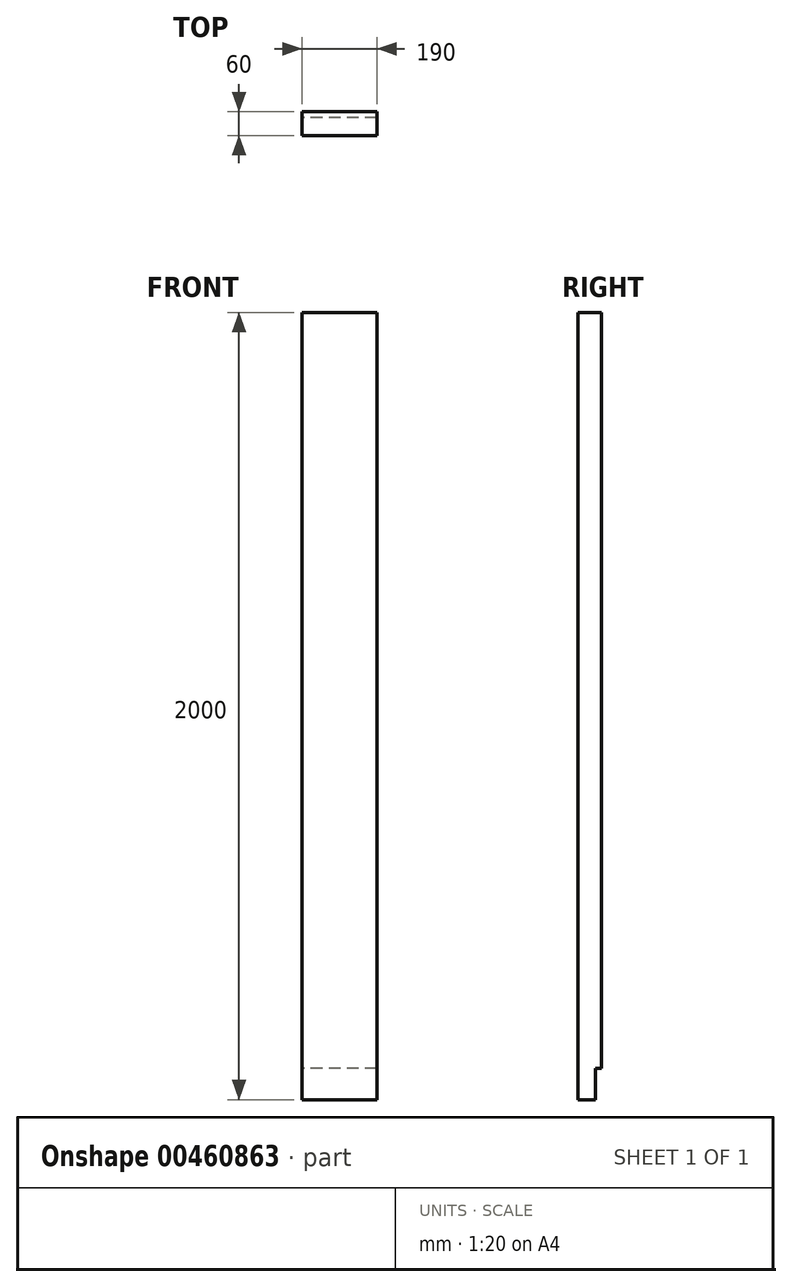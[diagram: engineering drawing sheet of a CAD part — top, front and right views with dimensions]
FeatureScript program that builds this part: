
annotation { "Feature Type Name" : "Feature", "Feature Type Description" : "" }
export const myFeature = defineFeature(function(context is Context, id is Id, definition is map)
    precondition{}
    {
        {
            var Q0;
            Q0=qCreatedBy(makeId("Front.planeOp"),FACE);
            var sketch = newSketch(context, id + "F0", { "sketchPlane" : qUnion([Q0])});
            skLineSegment(sketch, "E0.bottom", {"start": v(190, -3224.72) * mm, "end": v(0, -3224.72) * mm});
            skLineSegment(sketch, "E0.top", {"start": v(190, -5224.72) * mm, "end": v(0, -5224.72) * mm});
            skLineSegment(sketch, "E0.left", {"start": v(190, -3224.72) * mm, "end": v(190, -5224.72) * mm});
            skLineSegment(sketch, "E0.right", {"start": v(0, -3224.72) * mm, "end": v(0, -5224.72) * mm});
            skSolve(sketch);
        }
        {
            var Q0;
            Q0=makeQuery(id+"F0.imprint","IMPRINT",FACE,{"disambiguationData":[TD([[makeQuery(id+"F0.imprint","IMPRINT",EDGE,{"derivedFrom":sQuery(id+"F0.wireOp",EDGE,"E0.bottom")}),1.0]])]});
            extrude(context, id + "F1", {"entities" : qUnion([Q0]), "depth" : 60 * mm});
        }
        {
            var Q0;
            Q0=makeQuery(id+"F1.opExtrude","SWEPT_FACE",FACE,{"disambiguationData":[OSD([sQuery(id+"F0.wireOp",EDGE,"E0.right")])]});
            var sketch = newSketch(context, id + "F2", { "sketchPlane" : qUnion([Q0])});
            skLineSegment(sketch, "E1.bottom", {"start": v(15, -5144.72) * mm, "end": v(0, -5144.72) * mm});
            skLineSegment(sketch, "E1.top", {"start": v(15, -5224.72) * mm, "end": v(0, -5224.72) * mm});
            skLineSegment(sketch, "E1.left", {"start": v(15, -5144.72) * mm, "end": v(15, -5224.72) * mm});
            skLineSegment(sketch, "E1.right", {"start": v(0, -5144.72) * mm, "end": v(0, -5224.72) * mm});
            skSolve(sketch);
        }
        {
            var Q0;
            Q0 = qSketchRegion(id + "F2", true);
            extrude(context, id + "F3", {"entities" : qUnion([Q0]), "operationType" : NewBodyOperationType.REMOVE, "endBound" : BoundingType.THROUGH_ALL, "oppositeDirection" : true, "depth" : 25 * mm});
        }
    });
